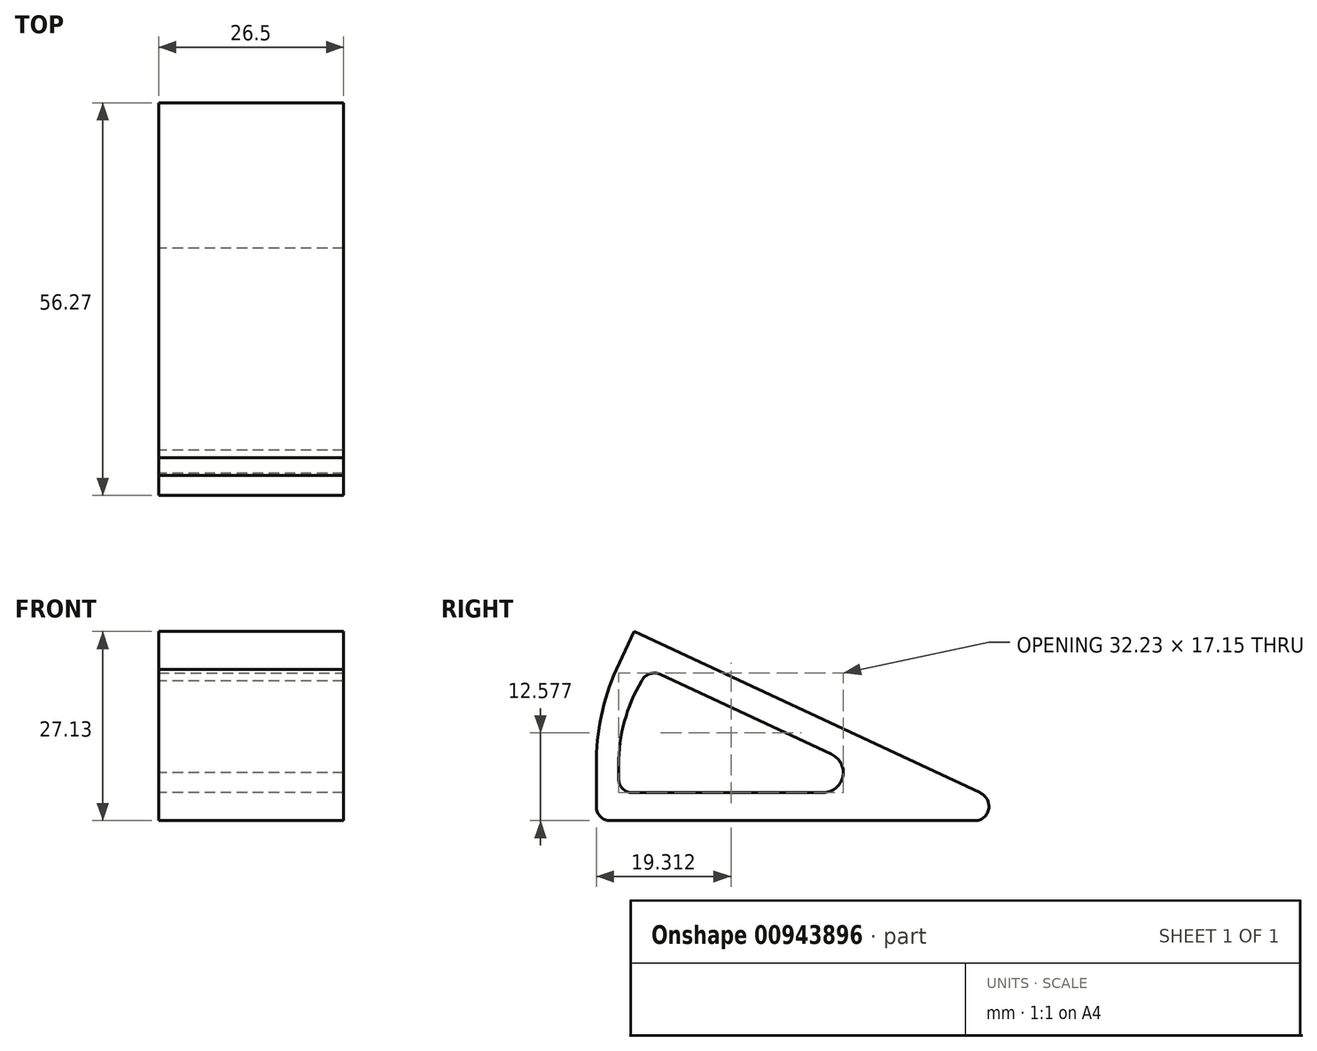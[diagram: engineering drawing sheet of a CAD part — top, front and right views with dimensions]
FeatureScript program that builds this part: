
annotation { "Feature Type Name" : "Feature", "Feature Type Description" : "" }
export const myFeature = defineFeature(function(context is Context, id is Id, definition is map)
    precondition{}
    {
        {
            var Q0;
            Q0=qCreatedBy(makeId("Right.planeOp"),FACE);
            var sketch = newSketch(context, id + "F0", { "sketchPlane" : qUnion([Q0])});
            skLineSegment(sketch, "E0", {"start": v(-24.95, 20.9) * mm, "end": v(24.65, -2.22) * mm});
            skLineSegment(sketch, "E1", {"start": v(-24.95, 20.9) * mm, "end": v(-27.49, 15.47) * mm});
            skLineSegment(sketch, "E2", {"start": v(-27.49, 15.47) * mm, "end": v(-23.86, 13.78) * mm});
            skLineSegment(sketch, "E3", {"start": v(-23.86, 13.78) * mm, "end": v(-23.02, 15.6) * mm});
            skLineSegment(sketch, "E4", {"start": v(-23.02, 15.6) * mm, "end": v(7.8, 1.22) * mm});
            skLineSegment(sketch, "E5", {"start": v(1.2, -2.22) * mm, "end": v(-27.15, -2.22) * mm});
            skLineSegment(sketch, "E6", {"start": v(24.65, -6.22) * mm, "end": v(-30.35, -6.22) * mm});
            skArc(sketch, "E7", {"start": v(24.65, -6.22) * mm, "mid": v(25.92, -4.22) * mm, "end": v(24.65, -2.22) * mm});
            skLineSegment(sketch, "E8", {"start": v(7.8, 1.22) * mm, "end": v(15.17, -2.21) * mm});
            skLineSegment(sketch, "E9", {"start": v(1.2, -2.22) * mm, "end": v(15.17, -2.21) * mm});
            skPoint(sketch, "E10", {"position": v(-7.61, 8.4) * mm});
            skLineSegment(sketch, "E11", {"start": v(-30.35, -6.22) * mm, "end": v(-30.35, 1.78) * mm});
            skLineSegment(sketch, "E12", {"start": v(-30.35, 1.78) * mm, "end": v(-27.15, 1.78) * mm});
            skLineSegment(sketch, "E13", {"start": v(-27.15, 1.78) * mm, "end": v(-27.15, -2.22) * mm});
            skArc(sketch, "E14", {"start": v(-27.49, 15.47) * mm, "mid": v(-29.63, 8.77) * mm, "end": v(-30.35, 1.78) * mm});
            skArc(sketch, "E15", {"start": v(-23.86, 13.78) * mm, "mid": v(-26.31, 8) * mm, "end": v(-27.15, 1.78) * mm});
            skPoint(sketch, "E16.start.orphan", {"position": v(-10.87, 9.93) * mm});
            skPoint(sketch, "E17.end.orphan", {"position": v(5.08, 2.5) * mm});
            skLineSegment(sketch, "E18", {"start": v(5.08, 2.5) * mm, "end": v(5.08, -2.22) * mm});
            skSolve(sketch);
        }
        {
            var Q0;
            Q0=makeQuery(id+"F0.imprint","IMPRINT",FACE,{"disambiguationData":[TD([[makeQuery(id+"F0.imprint","IMPRINT",EDGE,{"derivedFrom":sQuery(id+"F0.wireOp",EDGE,"E0")}),-1.0]])]});
            var Q1;
            {var subQ4=sQuery(id+"F0.wireOp",EDGE,"E16");Q1=makeQuery(id+"F0.imprint","IMPRINT",FACE,{"disambiguationData":[TD([[makeQuery(id+"F0.imprint","IMPRINT",EDGE,{"derivedFrom":subQ4}),-1.0]])]});}
            var Q2;
            Q2=makeQuery(id+"F0.imprint","IMPRINT",FACE,{"disambiguationData":[TD([[makeQuery(id+"F0.imprint","IMPRINT",EDGE,{"derivedFrom":sQuery(id+"F0.wireOp",EDGE,"E2")}),-1.0]])]});
            var Q3;
            {var subQ0=sQuery(id+"F0.wireOp",EDGE,"E8");Q3=makeQuery(id+"F0.imprint","IMPRINT",FACE,{"disambiguationData":[TD([[makeQuery(id+"F0.imprint","IMPRINT",EDGE,{"derivedFrom":subQ0}),-1.0]])]});}
            extrude(context, id + "F1", {"entities" : qUnion([Q0, Q1, Q2, Q3]), "endBound" : BoundingType.SYMMETRIC, "depth" : 26.5 * mm, "offsetDistance" : 25 * mm});
        }
        {
            var Q0;
            Q0=makeQuery(id+"F0.imprint","IMPRINT",FACE,{"disambiguationData":[TD([[makeQuery(id+"F0.imprint","IMPRINT",EDGE,{"derivedFrom":sQuery(id+"F0.wireOp",EDGE,"QRtXZlLI-DyVu-glti-b1aF-PIUHgjWpgFsE")}),-1.0]])]});
            var Q1;
            Q1=makeQuery(id+"F0.imprint","IMPRINT",FACE,{"disambiguationData":[TD([[makeQuery(id+"F0.imprint","IMPRINT",EDGE,{"derivedFrom":sQuery(id+"F0.wireOp",EDGE,"E5")}),1.0]])]});
            var Q2;
            {var subQ0=sQuery(id+"F0.wireOp",EDGE,"KnKN6Aqi-Ftqc-PoKH-mqI8-RxSOGZB0yrOI");Q2=makeQuery(id+"F0.imprint","IMPRINT",FACE,{"disambiguationData":[TD([[makeQuery(id+"F0.imprint","IMPRINT",EDGE,{"derivedFrom":subQ0}),1.0]])]});}
            extrude(context, id + "F2", {"entities" : qUnion([Q0, Q1, Q2]), "operationType" : NewBodyOperationType.ADD, "endBound" : BoundingType.SYMMETRIC, "depth" : 26.5 * mm, "offsetDistance" : 25 * mm});
        }
        {
            var Q0;
            Q0=makeQuery(id+"F1.opExtrude","SWEPT_EDGE",EDGE,{"disambiguationData":[OSD([sQuery(id+"F0.wireOp",EDGE,"E3"),sQuery(id+"F0.wireOp",EDGE,"E4")])]});
            var Q1;
            Q1=makeQuery(id+"F1.opExtrude","SWEPT_EDGE",EDGE,{"disambiguationData":[OSD([sQuery(id+"F0.wireOp",EDGE,"E0"),sQuery(id+"F0.wireOp",EDGE,"E7")])]});
            var Q2;
            Q2=makeQuery(id+"F1.opExtrude","SWEPT_EDGE",EDGE,{"disambiguationData":[OSD([sQuery(id+"F0.wireOp",EDGE,"E6"),sQuery(id+"F0.wireOp",EDGE,"E7")])]});
            fillet(context, id + "F3", {"entities" : qUnion([Q0, Q1, Q2]), "radius" : 2 * mm, "tangentPropagation" : true, "allowEdgeOverflow" : false});
        }
        {
            var Q0;
            Q0=makeQuery(id+"F1.opExtrude","SWEPT_EDGE",EDGE,{"disambiguationData":[OSD([sQuery(id+"F0.wireOp",EDGE,"E5"),sQuery(id+"F0.wireOp",EDGE,"E13")])]});
            var Q1;
            Q1=makeQuery(id+"F1.opExtrude","SWEPT_EDGE",EDGE,{"disambiguationData":[OSD([sQuery(id+"F0.wireOp",EDGE,"E6"),sQuery(id+"F0.wireOp",EDGE,"E11")])]});
            var Q2;
            Q2=makeQuery(id+"F1.opExtrude","SWEPT_EDGE",EDGE,{"disambiguationData":[OSD([sQuery(id+"F0.wireOp",EDGE,"E11"),sQuery(id+"F0.wireOp",EDGE,"E12")])]});
            fillet(context, id + "F4", {"entities" : qUnion([Q0, Q1, Q2]), "radius" : 2 * mm, "tangentPropagation" : true, "allowEdgeOverflow" : false});
        }
        {
            var Q0;
            Q0=makeQuery(id+"F1.opExtrude","SWEPT_EDGE",EDGE,{"disambiguationData":[OSD([sQuery(id+"F0.wireOp",EDGE,"E9"),sQuery(id+"F0.wireOp",EDGE,"E18")])]});
            var Q1;
            Q1=makeQuery(id+"F1.opExtrude","SWEPT_EDGE",EDGE,{"disambiguationData":[OSD([sQuery(id+"F0.wireOp",EDGE,"E4"),sQuery(id+"F0.wireOp",EDGE,"E18")])]});
            fillet(context, id + "F5", {"entities" : qUnion([Q0, Q1]), "radius" : 3 * mm, "tangentPropagation" : true, "allowEdgeOverflow" : false});
        }
    });
